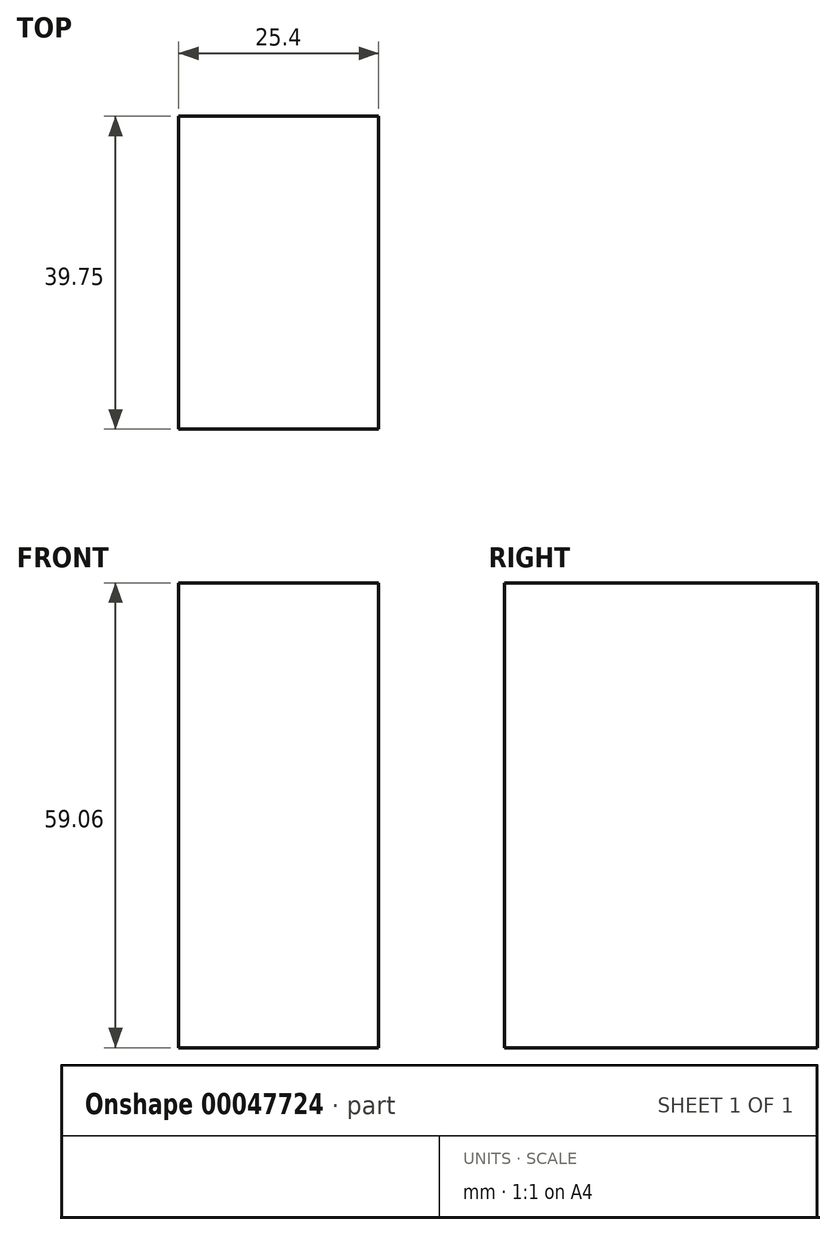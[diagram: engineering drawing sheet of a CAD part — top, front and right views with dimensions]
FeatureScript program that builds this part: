
annotation { "Feature Type Name" : "Feature", "Feature Type Description" : "" }
export const myFeature = defineFeature(function(context is Context, id is Id, definition is map)
    precondition{}
    {
        {
            var Q0;
            Q0=qCreatedBy(makeId("Right.planeOp"),FACE);
            var sketch = newSketch(context, id + "F0", { "sketchPlane" : qUnion([Q0])});
            skLineSegment(sketch, "E0.bottom", {"start": v(0, 0) * mm, "end": v(-39.75, 0) * mm});
            skLineSegment(sketch, "E0.top", {"start": v(0, 59.06) * mm, "end": v(-39.75, 59.06) * mm});
            skLineSegment(sketch, "E0.left", {"start": v(0, 0) * mm, "end": v(0, 59.06) * mm});
            skLineSegment(sketch, "E0.right", {"start": v(-39.75, 0) * mm, "end": v(-39.75, 59.06) * mm});
            skSolve(sketch);
        }
        {
            var Q0;
            Q0=makeQuery(id+"F0.imprint","IMPRINT",FACE,{"disambiguationData":[TD([[makeQuery(id+"F0.imprint","IMPRINT",EDGE,{"derivedFrom":sQuery(id+"F0.wireOp",EDGE,"E0.bottom")}),-1.0]])]});
            extrude(context, id + "F1", {"entities" : qUnion([Q0]), "depth" : 25.4 * mm});
        }
    });
